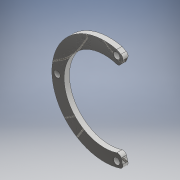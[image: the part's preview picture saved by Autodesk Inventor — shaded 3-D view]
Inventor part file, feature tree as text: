
AUTODESK INVENTOR PART (.ipt)
format: ipt  version: 2017 (Build 210142000, 142)  size: 144,384 bytes
history: native  units: mm
features: extrude x1, fillet x1, sketch x1
ambient origin geometry x8: Origin, YZ Plane, XZ Plane, XY Plane, X Axis, Y Axis, Z Axis, Center Point
bodies: Solid1 (feature_tree)
feature tree (3):
  extrude  "Extrusion1"  Depth=2.0mm
  fillet  "Fillet1"  Radius=30.0mm
  sketch  "Sketch1"  dims[d14=54.0mm d16=46.0mm d17=30.0mm d19=3.5mm d20=3.5mm d21=7.0mm d22=3.5mm d23=3.0mm d24=0.0mm d25=2.0mm]
